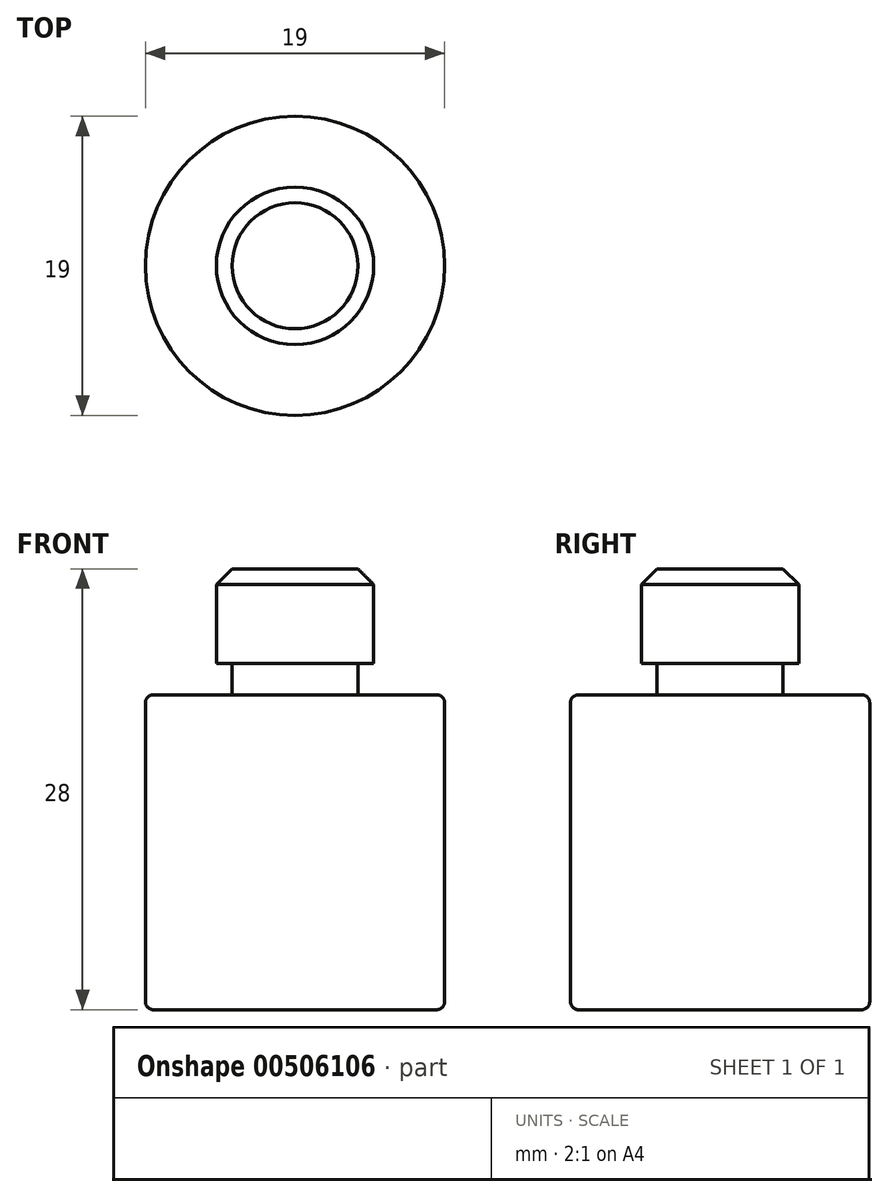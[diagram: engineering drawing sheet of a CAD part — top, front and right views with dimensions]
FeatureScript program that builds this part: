
annotation { "Feature Type Name" : "Feature", "Feature Type Description" : "" }
export const myFeature = defineFeature(function(context is Context, id is Id, definition is map)
    precondition{}
    {
        {
            var Q0;
            Q0=qCreatedBy(makeId("Top.planeOp"),FACE);
            var sketch = newSketch(context, id + "F0", { "sketchPlane" : qUnion([Q0])});
            skCircle(sketch, "E0", {"center": v(0, 0) * mm, "radius": 9.5 * mm});
            skSolve(sketch);
        }
        {
            var Q0;
            Q0 = qSketchRegion(id + "F0", true);
            extrude(context, id + "F1", {"entities" : qUnion([Q0]), "oppositeDirection" : true, "depth" : 20 * mm});
        }
        {
            var Q0;
            Q0=makeQuery(id+"F1.opExtrude","CAP_FACE",FACE,{"disambiguationData":[OSD([sQuery(id+"F0.wireOp",EDGE,"E0")])],"isStart":true});
            var sketch = newSketch(context, id + "F2", { "sketchPlane" : qUnion([Q0])});
            skCircle(sketch, "E1", {"center": v(0, 0) * mm, "radius": 5 * mm});
            skSolve(sketch);
        }
        {
            var Q0;
            Q0 = qSketchRegion(id + "F2", true);
            extrude(context, id + "F3", {"entities" : qUnion([Q0]), "operationType" : NewBodyOperationType.ADD, "depth" : 8 * mm});
        }
        {
            var Q0;
            Q0=makeQuery(id+"F1.opExtrude","CAP_EDGE",EDGE,{"disambiguationData":[OSD([sQuery(id+"F0.wireOp",EDGE,"E0")])],"isStart":false});
            var Q1;
            Q1=makeQuery(id+"F1.opExtrude","CAP_EDGE",EDGE,{"disambiguationData":[OSD([sQuery(id+"F0.wireOp",EDGE,"E0")])],"isStart":true});
            fillet(context, id + "F4", {"entities" : qUnion([Q0, Q1]), "radius" : 0.5 * mm, "tangentPropagation" : true, "allowEdgeOverflow" : false});
        }
        {
            var Q0;
            Q0=makeQuery(id+"F3.opExtrude","CAP_EDGE",EDGE,{"disambiguationData":[OSD([sQuery(id+"F2.wireOp",EDGE,"E1")])],"isStart":false});
            chamfer(context, id + "F5", {"entities" : qUnion([Q0]), "width" : 1 * mm, "tangentPropagation" : true});
        }
        {
            var Q0;
            Q0=qCreatedBy(makeId("Right.planeOp"),FACE);
            var sketch = newSketch(context, id + "F6", { "sketchPlane" : qUnion([Q0])});
            skLineSegment(sketch, "E2", {"start": v(-5, 0) * mm, "end": v(-5, 2) * mm});
            skLineSegment(sketch, "E3", {"start": v(0, 0) * mm, "end": v(0, 15.7) * mm, "construction": true});
            skLineSegment(sketch, "E4", {"start": v(-5, 0) * mm, "end": v(-4, 0) * mm});
            skLineSegment(sketch, "E5", {"start": v(-4, 2) * mm, "end": v(-4, 0) * mm});
            skLineSegment(sketch, "E6", {"start": v(-5, 2) * mm, "end": v(-4, 2) * mm});
            skSolve(sketch);
        }
        {
            var Q0;
            Q0 = qSketchRegion(id + "F6", true);
            var Q1;
            Q1=sQuery(id+"F6.wireOp",EDGE,"E3");
            revolve(context, id + "F7", {"operationType" : NewBodyOperationType.REMOVE, "entities" : qUnion([Q0]), "axis" : qUnion([Q1]), "revolveType" : RevolveType.FULL, "oppositeDirection" : true});
        }
    });
